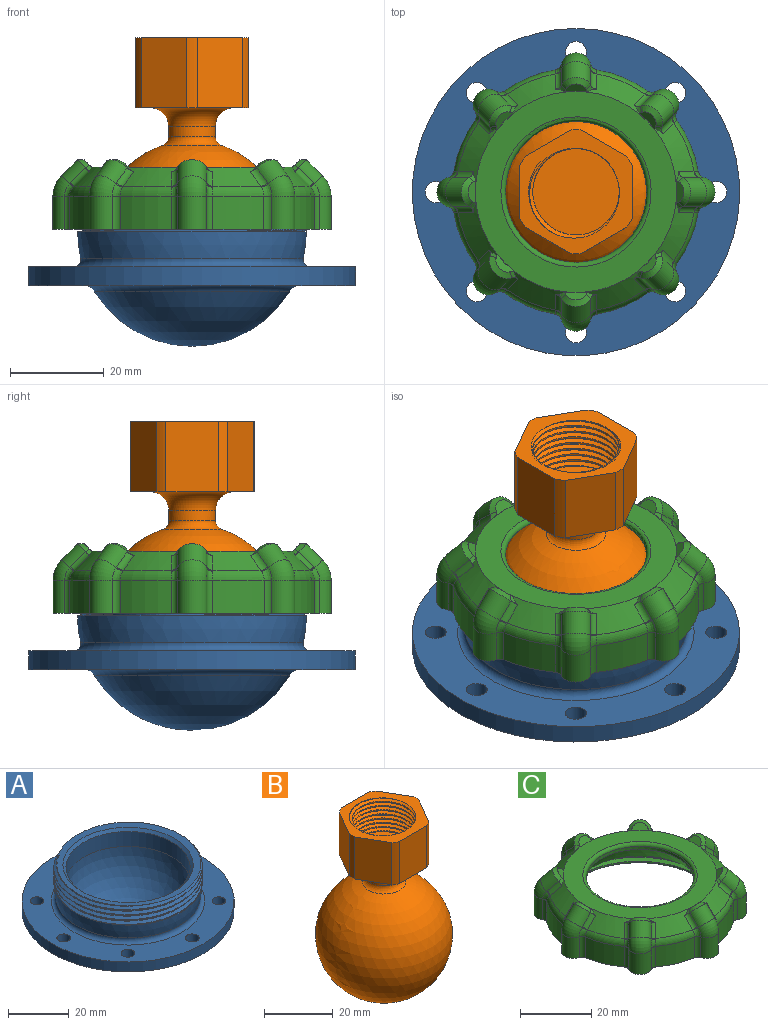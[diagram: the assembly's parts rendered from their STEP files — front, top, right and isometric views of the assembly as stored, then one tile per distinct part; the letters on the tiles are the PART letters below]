
ASSEMBLY  parts=3 mates=3
PART A: 24 faces, bbox 70.7x70.7x33 mm
  f0: cylinder r=35mm len=70mm, axis (0,0,-1), area 879.6mm2, adj f1,f2
  f1: plane 70x70mm, normal (0,0,1), area 1710.6mm2, adj f0,f3,f4,f5,f6,f7,f8,f9
  f2: plane 70x70mm, normal (0,0,-1), area 2046.7mm2, adj f0,f3,f4,f5,f6,f7,f8,f9
  f3: cylinder r=2.25mm len=4.5mm, axis (0,0,1), area 56.5mm2, adj f1,f2
  f4: cylinder r=2.25mm len=4.5mm, axis (0,0,1), area 56.5mm2, adj f1,f2
  f5: cylinder r=2.25mm len=4.5mm, axis (0,0,1), area 56.5mm2, adj f1,f2
  f6: cylinder r=2.25mm len=4.5mm, axis (0,0,1), area 56.5mm2, adj f1,f2
  f7: cylinder r=2.25mm len=4.5mm, axis (0,0,1), area 56.5mm2, adj f1,f2
  f8: cylinder r=2.25mm len=4.5mm, axis (0,0,1), area 56.5mm2, adj f1,f2
  f9: cylinder r=2.25mm len=4.5mm, axis (0,0,1), area 56.5mm2, adj f1,f2
  f10: cylinder r=2.25mm len=4.5mm, axis (0,0,1), area 56.5mm2, adj f1,f2
  f11: sphere r=24.5mm, area 1815.9mm2, adj f13
  f12: sphere r=24.5mm, area 870.3mm2, adj f14,f21,f23
  f13: torus R=23.09mm, axis (0,0,1), area 353.1mm2, adj f2,f11
  f14: cylinder r=24.5mm len=49mm, axis (0,0,-1), area 130.8mm2, adj f12,f16,f19,f20
  f15: cylinder r=20.5mm len=41mm, axis (0,0,-1), area 772.8mm2, adj f17,f22
  f16: plane 48.53x48.41mm, normal (0,0,1), area 338.8mm2, adj f14,f18,f19,f20,f22
  f17: sphere r=20.5mm, area 2640.5mm2, adj f15
  f18: bspline ~54.08x46.84mm, area 287.6mm2, adj f16,f19,f20,f21
  f19: bspline ~56.58x49mm, area 659.3mm2, adj f14,f16,f18,f21
  f20: bspline ~56.58x49mm, area 658.3mm2, adj f14,f16,f18,f21
  f21: plane 49.7x49.7mm, normal (0,0,1), area 94.8mm2, adj f12,f18,f19,f20
  f22: cone r=20.5mm half-angle=45deg, axis (0,0,1), area 186.6mm2, adj f15,f16
  f23: torus R=25.3mm, axis (0,0,1), area 412.6mm2, adj f1,f12
PART B: 24 faces, bbox 40.2x40.2x64.1 mm
  f0: cylinder r=13.25mm len=15mm, axis (0,0,-1), area 34.1mm2, adj f5,f7,f16,f21
  f1: cylinder r=13.25mm len=15mm, axis (0,0,-1), area 34.1mm2, adj f5,f7,f20,f21
  f2: cylinder r=13.25mm len=15mm, axis (0,0,-1), area 34.1mm2, adj f5,f7,f19,f20
  f3: cylinder r=13.25mm len=15mm, axis (0,0,-1), area 34.1mm2, adj f5,f7,f18,f19
  f4: cylinder r=13.25mm len=15mm, axis (0,0,-1), area 34.1mm2, adj f5,f7,f17,f18
  f5: plane 26.5x24mm, normal (0,0,-1), area 240.3mm2, adj f0,f1,f2,f3,f4,f10,f16,f17
  f6: plane 19.35x19.34mm, normal (0,0,1), area 290.4mm2, adj f12,f13,f14,f15
  f7: plane 26.67x24.17mm, normal (0,0,1), area 204.4mm2, adj f0,f1,f2,f3,f4,f10,f12,f13
  f8: sphere r=20mm, area 4895.9mm2, adj f11
  f9: cylinder r=5mm len=10mm, axis (0,0,-1), area 67.3mm2, adj f11,f22
  f10: cylinder r=13.25mm len=15mm, axis (0,0,-1), area 34.1mm2, adj f5,f7,f16,f17
  f11: torus R=7mm, axis (0,0,-1), area 85.9mm2, adj f8,f9
  f12: bspline ~23.24x20.12mm, area 94.6mm2, adj f6,f7,f14,f15
  f13: bspline ~20.09x20.06mm, area 476.1mm2, adj f6,f7,f14,f15
  f14: bspline ~23.39x20.26mm, area 110.4mm2, adj f6,f7,f12,f13
  f15: cylinder r=9.25mm len=18.5mm, axis (0,0,-1), area 135mm2, adj f6,f7,f12,f13
  f16: plane 15x9.73mm, normal (-0.87,0.5,0), area 168.5mm2, adj f0,f5,f7,f10
  f17: plane 15x9.73mm, normal (-0.87,-0.5,0), area 168.5mm2, adj f4,f5,f7,f10
  f18: plane 15x11.24mm, normal (0,-1,0), area 168.5mm2, adj f3,f4,f5,f7
  f19: plane 15x9.73mm, normal (0.87,-0.5,0), area 168.5mm2, adj f2,f3,f5,f7
  f20: plane 15x9.73mm, normal (0.87,0.5,0), area 168.5mm2, adj f1,f2,f5,f7
  f21: plane 15x11.24mm, normal (0,1,0), area 168.5mm2, adj f0,f1,f5,f7
  f22: torus R=9mm, axis (0,0,1), area 254.8mm2, adj f5,f9
  f23: sphere r=14mm, area 2463mm2
PART C: 154 faces, bbox 61.7x61.7x18.2 mm
  f0: cylinder r=26.5mm len=11.02mm, axis (0,0,-1), area 85mm2, adj f2,f22,f105,f117
  f1: cone r=26.5mm half-angle=45deg, axis (0,0,-1), area 59.2mm2, adj f2,f24,f57,f61,f108,f120,f135,f140
  f2: torus R=23.5mm, axis (0,0,1), area 27.6mm2, adj f0,f1,f106,f107,f118,f119
  f3: cylinder r=26.5mm len=11.02mm, axis (0,0,-1), area 85mm2, adj f5,f22,f97,f109
  f4: cone r=26.5mm half-angle=45deg, axis (0,0,-1), area 59.2mm2, adj f5,f24,f53,f57,f100,f112,f132,f137
  f5: torus R=23.5mm, axis (0,0,1), area 27.6mm2, adj f3,f4,f98,f99,f110,f111
  f6: cylinder r=26.5mm len=11.02mm, axis (0,0,-1), area 85mm2, adj f8,f22,f89,f101
  f7: cone r=26.5mm half-angle=45deg, axis (0,0,-1), area 59.2mm2, adj f8,f24,f49,f53,f92,f104,f129,f134
  f8: torus R=23.5mm, axis (0,0,1), area 27.6mm2, adj f6,f7,f90,f91,f102,f103
  f9: cylinder r=26.5mm len=11.02mm, axis (0,0,-1), area 85mm2, adj f11,f22,f81,f93
  f10: cone r=26.5mm half-angle=45deg, axis (0,0,-1), area 59.2mm2, adj f11,f24,f45,f49,f84,f96,f131,f144
  f11: torus R=23.5mm, axis (0,0,1), area 27.6mm2, adj f9,f10,f82,f83,f94,f95
  f12: cylinder r=26.5mm len=11.02mm, axis (0,0,-1), area 85mm2, adj f14,f22,f73,f85
  f13: cone r=26.5mm half-angle=45deg, axis (0,0,-1), area 59.2mm2, adj f14,f24,f41,f45,f76,f88,f146,f150
  f14: torus R=23.5mm, axis (0,0,1), area 27.6mm2, adj f12,f13,f74,f75,f86,f87
  f15: cylinder r=26.5mm len=11.02mm, axis (0,0,-1), area 85mm2, adj f17,f22,f65,f77
  f16: cone r=26.5mm half-angle=45deg, axis (0,0,-1), area 59.2mm2, adj f17,f24,f37,f41,f68,f80,f147,f152
  f17: torus R=23.5mm, axis (0,0,1), area 27.6mm2, adj f15,f16,f66,f67,f78,f79
  f18: cylinder r=26.5mm len=11.02mm, axis (0,0,-1), area 85mm2, adj f20,f22,f69,f121
  f19: cone r=26.5mm half-angle=45deg, axis (0,0,-1), area 59.2mm2, adj f20,f24,f33,f37,f72,f124,f141,f149
  f20: torus R=23.5mm, axis (0,0,1), area 27.6mm2, adj f18,f19,f70,f71,f122,f123
  f21: plane 48.52x48.52mm, normal (0,0,-1), area 702.5mm2, adj f26,f27,f28,f29,f30
  f22: plane 59.9x59.9mm, normal (0,0,-1), area 539.1mm2, adj f0,f3,f6,f9,f12,f15,f18,f23
  f23: cylinder r=26.5mm len=11.02mm, axis (0,0,-1), area 85mm2, adj f22,f32,f113,f125
  f24: plane 43x43mm, normal (0,0,1), area 641.4mm2, adj f1,f4,f7,f10,f13,f16,f19,f31
  f25: cylinder r=15.06mm len=30.13mm, axis (0,0,-1), area 94.7mm2, adj f26,f153
  f26: cone r=18.75mm half-angle=37.5deg, axis (0,0,-1), area 643.1mm2, adj f21,f25
  f27: bspline ~56.77x49.17mm, area 614.3mm2, adj f21,f22,f29,f30
  f28: bspline ~49.13x49.11mm, area 644mm2, adj f21,f22,f29,f30
  f29: bspline ~56.98x49.35mm, area 145.6mm2, adj f21,f22,f27,f28
  f30: cylinder r=23.5mm len=47mm, axis (0,0,1), area 242.3mm2, adj f21,f22,f27,f28
  f31: cone r=26.5mm half-angle=45deg, axis (0,0,-1), area 59.2mm2, adj f24,f32,f33,f61,f116,f128,f138,f143
  f32: torus R=23.5mm, axis (0,0,1), area 27.6mm2, adj f23,f31,f114,f115,f126,f127
  f33: plane 4.96x1.71mm, normal (-0.71,0,0.71), area 8.2mm2, adj f19,f31,f141,f142,f143
  f34: cylinder r=3.25mm len=7.06mm, axis (0,0,1), area 61.2mm2, adj f22,f35,f121,f125
  f35: torus R=3mm, axis (0,-1,0), area 36.3mm2, adj f34,f36,f122,f126
  f36: cylinder r=3.25mm len=6.3mm, axis (-0.71,0,0.71), area 41.3mm2, adj f35,f123,f124,f127,f128,f142
  f37: plane 3.78x3.78mm, normal (-0.5,-0.5,0.71), area 8.2mm2, adj f16,f19,f147,f148,f149
  f38: cylinder r=3.25mm len=7.06mm, axis (0,0,1), area 61.2mm2, adj f22,f39,f65,f69
  f39: torus R=3mm, axis (0.71,-0.71,0), area 36.3mm2, adj f38,f40,f66,f70
  f40: cylinder r=3.25mm len=7.05mm, axis (-0.5,-0.5,0.71), area 41.3mm2, adj f39,f67,f68,f71,f72,f148
  f41: plane 4.96x1.71mm, normal (0,-0.71,0.71), area 8.2mm2, adj f13,f16,f150,f151,f152
  f42: cylinder r=3.25mm len=7.06mm, axis (0,0,1), area 61.2mm2, adj f22,f43,f73,f77
  f43: torus R=3mm, axis (1,0,0), area 36.3mm2, adj f42,f44,f74,f78
  f44: cylinder r=3.25mm len=6.3mm, axis (0,-0.71,0.71), area 41.3mm2, adj f43,f75,f76,f79,f80,f151
  f45: plane 3.78x3.78mm, normal (0.5,-0.5,0.71), area 8.2mm2, adj f10,f13,f144,f145,f146
  f46: cylinder r=3.25mm len=7.06mm, axis (0,0,1), area 61.2mm2, adj f22,f47,f81,f85
  f47: torus R=3mm, axis (0.71,0.71,0), area 36.3mm2, adj f46,f48,f82,f86
  f48: cylinder r=3.25mm len=7.05mm, axis (0.5,-0.5,0.71), area 41.3mm2, adj f47,f83,f84,f87,f88,f145
  f49: plane 4.96x1.71mm, normal (0.71,0,0.71), area 8.2mm2, adj f7,f10,f129,f130,f131
  f50: cylinder r=3.25mm len=7.06mm, axis (0,0,1), area 61.2mm2, adj f22,f51,f89,f93
  f51: torus R=3mm, axis (0,1,0), area 36.3mm2, adj f50,f52,f90,f94
  f52: cylinder r=3.25mm len=6.3mm, axis (0.71,0,0.71), area 41.3mm2, adj f51,f91,f92,f95,f96,f130
  f53: plane 3.78x3.78mm, normal (0.5,0.5,0.71), area 8.2mm2, adj f4,f7,f132,f133,f134
  f54: cylinder r=3.25mm len=7.06mm, axis (0,0,1), area 61.2mm2, adj f22,f55,f97,f101
  f55: torus R=3mm, axis (-0.71,0.71,0), area 36.3mm2, adj f54,f56,f98,f102
  f56: cylinder r=3.25mm len=7.05mm, axis (0.5,0.5,0.71), area 41.3mm2, adj f55,f99,f100,f103,f104,f133
  f57: plane 4.96x1.71mm, normal (0,0.71,0.71), area 8.2mm2, adj f1,f4,f135,f136,f137
  f58: cylinder r=3.25mm len=7.06mm, axis (0,0,1), area 61.2mm2, adj f22,f59,f105,f109
  f59: torus R=3mm, axis (-1,0,0), area 36.3mm2, adj f58,f60,f106,f110
  f60: cylinder r=3.25mm len=6.3mm, axis (0,0.71,0.71), area 41.3mm2, adj f59,f107,f108,f111,f112,f136
  f61: plane 3.78x3.78mm, normal (-0.5,0.5,0.71), area 8.2mm2, adj f1,f31,f138,f139,f140
  f62: cylinder r=3.25mm len=7.06mm, axis (0,0,1), area 61.2mm2, adj f22,f63,f113,f117
  f63: torus R=3mm, axis (-0.71,-0.71,0), area 36.3mm2, adj f62,f64,f114,f118
  f64: cylinder r=3.25mm len=7.05mm, axis (-0.5,0.5,0.71), area 41.3mm2, adj f63,f115,f116,f119,f120,f139
  f65: cylinder r=1.5mm len=7.06mm, axis (0,0,-1), area 12.4mm2, adj f15,f22,f38,f66
  f66: bspline ~4.02x2.6mm, area 4.4mm2, adj f17,f39,f65,f67
  f67: bspline ~2.06x1.6mm, area 0.4mm2, adj f17,f40,f66,f68
  f68: bspline ~9.69x7.81mm, area 8.1mm2, adj f16,f40,f67,f147
  f69: cylinder r=1.5mm len=7.06mm, axis (0,0,-1), area 12.4mm2, adj f18,f22,f38,f70
  f70: bspline ~4.02x2.6mm, area 4.4mm2, adj f20,f39,f69,f71
  f71: bspline ~2.06x1.6mm, area 0.4mm2, adj f20,f40,f70,f72
  f72: bspline ~9.69x7.81mm, area 8.1mm2, adj f19,f40,f71,f149
  f73: cylinder r=1.5mm len=7.06mm, axis (0,0,-1), area 12.4mm2, adj f12,f22,f42,f74
  f74: bspline ~4.02x2.41mm, area 4.4mm2, adj f14,f43,f73,f75
  f75: bspline ~1.62x1.6mm, area 0.4mm2, adj f14,f44,f74,f76
  f76: bspline ~9.78x9.69mm, area 8.1mm2, adj f13,f44,f75,f150
  f77: cylinder r=1.5mm len=7.06mm, axis (0,0,-1), area 12.4mm2, adj f15,f22,f42,f78
  f78: bspline ~4.02x2.41mm, area 4.4mm2, adj f17,f43,f77,f79
  f79: bspline ~1.62x1.6mm, area 0.4mm2, adj f17,f44,f78,f80
  f80: bspline ~9.78x9.69mm, area 8.1mm2, adj f16,f44,f79,f152
  f81: cylinder r=1.5mm len=7.06mm, axis (0,0,-1), area 12.4mm2, adj f9,f22,f46,f82
  f82: bspline ~4.02x2.6mm, area 4.4mm2, adj f11,f47,f81,f83
  f83: bspline ~2.06x1.6mm, area 0.4mm2, adj f11,f48,f82,f84
  f84: bspline ~9.69x7.81mm, area 8.1mm2, adj f10,f48,f83,f144
  f85: cylinder r=1.5mm len=7.06mm, axis (0,0,-1), area 12.4mm2, adj f12,f22,f46,f86
  f86: bspline ~4.02x2.6mm, area 4.4mm2, adj f14,f47,f85,f87
  f87: bspline ~2.06x1.6mm, area 0.4mm2, adj f14,f48,f86,f88
  f88: bspline ~9.69x7.81mm, area 8.1mm2, adj f13,f48,f87,f146
  f89: cylinder r=1.5mm len=7.06mm, axis (0,0,-1), area 12.4mm2, adj f6,f22,f50,f90
  f90: bspline ~4.02x2.41mm, area 4.4mm2, adj f8,f51,f89,f91
  f91: bspline ~1.62x1.6mm, area 0.4mm2, adj f8,f52,f90,f92
  f92: bspline ~9.78x9.69mm, area 8.1mm2, adj f7,f52,f91,f129
  f93: cylinder r=1.5mm len=7.06mm, axis (0,0,-1), area 12.4mm2, adj f9,f22,f50,f94
  f94: bspline ~4.02x2.41mm, area 4.4mm2, adj f11,f51,f93,f95
  f95: bspline ~1.62x1.6mm, area 0.4mm2, adj f11,f52,f94,f96
  f96: bspline ~9.78x9.69mm, area 8.1mm2, adj f10,f52,f95,f131
  f97: cylinder r=1.5mm len=7.06mm, axis (0,0,-1), area 12.4mm2, adj f3,f22,f54,f98
  f98: bspline ~4.02x2.6mm, area 4.4mm2, adj f5,f55,f97,f99
  f99: bspline ~2.06x1.6mm, area 0.4mm2, adj f5,f56,f98,f100
  f100: bspline ~9.69x7.81mm, area 8.1mm2, adj f4,f56,f99,f132
  f101: cylinder r=1.5mm len=7.06mm, axis (0,0,-1), area 12.4mm2, adj f6,f22,f54,f102
  f102: bspline ~4.02x2.6mm, area 4.4mm2, adj f8,f55,f101,f103
  f103: bspline ~2.06x1.6mm, area 0.4mm2, adj f8,f56,f102,f104
  f104: bspline ~9.69x7.81mm, area 8.1mm2, adj f7,f56,f103,f134
  f105: cylinder r=1.5mm len=7.06mm, axis (0,0,-1), area 12.4mm2, adj f0,f22,f58,f106
  f106: bspline ~4.02x2.41mm, area 4.4mm2, adj f2,f59,f105,f107
  f107: bspline ~1.62x1.6mm, area 0.4mm2, adj f2,f60,f106,f108
  f108: bspline ~9.78x9.69mm, area 8.1mm2, adj f1,f60,f107,f135
  f109: cylinder r=1.5mm len=7.06mm, axis (0,0,-1), area 12.4mm2, adj f3,f22,f58,f110
  f110: bspline ~4.02x2.41mm, area 4.4mm2, adj f5,f59,f109,f111
  f111: bspline ~1.62x1.6mm, area 0.4mm2, adj f5,f60,f110,f112
  f112: bspline ~9.78x9.69mm, area 8.1mm2, adj f4,f60,f111,f137
  f113: cylinder r=1.5mm len=7.06mm, axis (0,0,-1), area 12.4mm2, adj f22,f23,f62,f114
  f114: bspline ~4.02x2.6mm, area 4.4mm2, adj f32,f63,f113,f115
  f115: bspline ~2.06x1.6mm, area 0.4mm2, adj f32,f64,f114,f116
  f116: bspline ~9.69x7.81mm, area 8.1mm2, adj f31,f64,f115,f138
  f117: cylinder r=1.5mm len=7.06mm, axis (0,0,-1), area 12.4mm2, adj f0,f22,f62,f118
  f118: bspline ~4.02x2.6mm, area 4.4mm2, adj f2,f63,f117,f119
  f119: bspline ~2.06x1.6mm, area 0.4mm2, adj f2,f64,f118,f120
  f120: bspline ~9.69x7.81mm, area 8.1mm2, adj f1,f64,f119,f140
  f121: cylinder r=1.5mm len=7.06mm, axis (0,0,-1), area 12.4mm2, adj f18,f22,f34,f122
  f122: bspline ~4.02x2.41mm, area 4.4mm2, adj f20,f35,f121,f123
  f123: bspline ~1.62x1.6mm, area 0.4mm2, adj f20,f36,f122,f124
  f124: bspline ~9.78x9.69mm, area 8.1mm2, adj f19,f36,f123,f141
  f125: cylinder r=1.5mm len=7.06mm, axis (0,0,-1), area 12.4mm2, adj f22,f23,f34,f126
  f126: bspline ~4.02x2.41mm, area 4.4mm2, adj f32,f35,f125,f127
  f127: bspline ~1.62x1.6mm, area 0.4mm2, adj f32,f36,f126,f128
  f128: bspline ~9.78x9.69mm, area 8.1mm2, adj f31,f36,f127,f143
  f129: bspline ~2.21x2.2mm, area 1.4mm2, adj f7,f49,f92,f130
  f130: cone r=2.25mm half-angle=45deg, axis (-0.71,0,-0.71), area 10.3mm2, adj f49,f52,f129,f131
  f131: bspline ~2.3x2.22mm, area 1.4mm2, adj f10,f49,f96,f130
  f132: bspline ~2.4x1.77mm, area 1.4mm2, adj f4,f53,f100,f133
  f133: cone r=2.25mm half-angle=45deg, axis (-0.5,-0.5,-0.71), area 10.3mm2, adj f53,f56,f132,f134
  f134: bspline ~2.51x2.03mm, area 1.4mm2, adj f7,f53,f104,f133
  f135: bspline ~2.21x2.2mm, area 1.4mm2, adj f1,f57,f108,f136
  f136: cone r=2.25mm half-angle=45deg, axis (0,-0.71,-0.71), area 10.3mm2, adj f57,f60,f135,f137
  f137: bspline ~2.3x2.22mm, area 1.4mm2, adj f4,f57,f112,f136
  f138: bspline ~2.4x1.77mm, area 1.4mm2, adj f31,f61,f116,f139
  f139: cone r=2.25mm half-angle=45deg, axis (0.5,-0.5,-0.71), area 10.3mm2, adj f61,f64,f138,f140
  f140: bspline ~2.51x2.03mm, area 1.4mm2, adj f1,f61,f120,f139
  f141: bspline ~2.21x2.2mm, area 1.4mm2, adj f19,f33,f124,f142
  f142: cone r=2.25mm half-angle=45deg, axis (0.71,0,-0.71), area 10.3mm2, adj f33,f36,f141,f143
  f143: bspline ~2.3x2.22mm, area 1.4mm2, adj f31,f33,f128,f142
  f144: bspline ~2.4x1.77mm, area 1.4mm2, adj f10,f45,f84,f145
  f145: cone r=2.25mm half-angle=45deg, axis (-0.5,0.5,-0.71), area 10.3mm2, adj f45,f48,f144,f146
  f146: bspline ~2.51x2.03mm, area 1.4mm2, adj f13,f45,f88,f145
  f147: bspline ~2.4x1.77mm, area 1.4mm2, adj f16,f37,f68,f148
  f148: cone r=2.25mm half-angle=45deg, axis (0.5,0.5,-0.71), area 10.3mm2, adj f37,f40,f147,f149
  f149: bspline ~2.51x2.03mm, area 1.4mm2, adj f19,f37,f72,f148
  f150: bspline ~2.21x2.2mm, area 1.4mm2, adj f13,f41,f76,f151
  f151: cone r=2.25mm half-angle=45deg, axis (0,0.71,-0.71), area 10.3mm2, adj f41,f44,f150,f152
  f152: bspline ~2.3x2.22mm, area 1.4mm2, adj f16,f41,f80,f151
  f153: torus R=16.06mm, axis (0,0,1), area 152.3mm2, adj f24,f25
PLACE A rot(axis=(0,0,1),90deg) t=(16.87,23.85,-4.55)mm fixed
PLACE B rot(axis=(0,0,1),90deg) t=(16.87,23.85,6.45)mm
PLACE C rot(axis=(0,0,1),45deg) t=(16.87,23.85,7.45)mm
MATE planar C.f21 <-> A.f16  axis (0,0,-1) through (15.36,23.85,13.95)mm
MATE parallel B.f7 <-> A.f5  axis (0,0,1) through (17.31,24.29,48.45)mm
MATE cylindrical A.f14 <-> C.f0  axis (0,0,-1) through (16.87,23.85,10.45)mm
